FCSTD DOCUMENT  (FreeCAD 0.19R24366 (Git))
Label: master
License: All rights reserved
LicenseURL: http://en.wikipedia.org/wiki/All_rights_reserved
objects: Spreadsheet::Sheet×1

FEATURE [Spreadsheet::Sheet] Spreadsheet  label="inputs"
  cells = A1=Top Edge Padding; B1(top_edge_padding)==10.4775mm; A2=Left Edge Padding; B2(left_edge_padding)==top_edge_padding; A3=Right Edge Padding; B3(right_edge_padding)==top_edge_padding; A4=Bottom Edge Padding; B4(bottom_edge_padding)==top_edge_padding; A5=Edge Fillet Radius; B5(edge_fillet_radius)==2mm; A6=Key Width; B6(key_width)==14mm; A7=Key Height; B7(key_height)==key_width; A8=Horizontal Key Spacing; B8(horizontal_key_spacing)==5.05mm; A9=Vertical Key Spacing; B9(vertical_key_spacing)==horizontal_key_spacing; A10=Mounting Hole Diameter; B10(mounting_hole_diameter)==3.1mm; A11=Switch Layer Thickness; B11(switch_layer_thickness)==3mm; A12=PCB Fillet Radius; B12(pcb_fillet_radius)==2mm; A13=PCB Top Edge Padding; B13(pcb_top_edge_padding)==2.53mm; A14=PCB Left Edge Padding; B14(pcb_left_edge_padding)==pcb_top_edge_padding; A15=PCB Right Edge Padding; B15(pcb_right_edge_padding)==pcb_top_edge_padding; A16=PCB Bottom Edge Padding; B16(pcb_bottom_edge_padding)==pcb_top_edge_padding; A17=PCB Inner Bottom Edge Padding; B17(pcb_inner_bottom_edge_padding)==pcb_top_edge_padding; A18=PCB Inner Right Edge Padding; B18(pcb_inner_right_edge_padding)==pcb_top_edge_padding; A19=Hyperpixel Width; B19(hyperpixel_width)==98mm; A20=Hyperpixel Height	; B20(hyperpixel_height)==58.2mm; A21=Hyperpixel Depth; B21(hyperpixel_depth)==5.7mm; A22=Hyperpixel Screen Width; B22(hyperpixel_screen_width)==hyperpixel_width; A23=Hyperpixel Top Hole Padding; B23(hyperpixel_top_hole_padding)==4.5mm; A24=HyperPixel Bottom Hole Padding; B24(hyperpixel_bottom_hole_padding)==4.7mm; A25=Hyperpixel Left Hole Padding; B25(hyperpixel_left_hole_padding)==25mm; A26=Hyperpixel Right Hole Padding; B26(hyperpixel_right_hole_padding)==15mm; A27=Hyperpixel Standoff Height; B27(hyperpixel_standoff_height)==17mm; A28=Hyperpixel Standoff Diameter; B28(hyperpixel_standoff_diameter)==5mm; A29=Joystick Top Edge Padding; B29(joystick_top_edge_padding)==vertical_key_spacing; A30=Joystick Left Edge Padding; B30(joystick_left_edge_padding)==0mm; A31=Joystick Right Edge Padding; B31(joystick_right_edge_padding)==horizontal_key_spacing; A32=Joystick Bottom Edge Padding; B32(joystick_bottom_edge_padding)==0mm; A33=Encoder Spacing; B33(encoder_spacing)==7mm; A34=Wall Thickness; B34(wall_thickness)==7.144mm; A35=Lower Layer Thickness; B35(lower_layer_thickness)==3mm; A36=Raspberry Pi 4 Mounting Hole Diameter; B36(raspberry_pi_4_mounting_hole_diameter)==2.75mm; A37=Open Layer Thickness; B37(open_layer_thickness)==3mm; A38=Bottom Layer Thickness; B38(bottom_layer_thickness)==3mm; A39=Top Layer Thickness; B39(top_layer_thickness)==3mm; A40=Top Layer Thin Thickness; B40(top_layer_thin_thickness)==1.5mm; A41=Hyperpixel Screen Padding; B41(hyperpixel_screen_padding)==1mm; A42=3D Printed Switch Layer Thickness; B42(switch_layer_thickness_3D_print)==1.5mm; A43=Encoder Unthreaded Shaft Diameter; B43(encoder_unthreaded_shaft_diameter)==6mm; A44=Encoder Threaded Shaft Diameter; B44(encoder_threaded_shaft_diameter)==6.75mm; A45=Encoder Unthreaded Shaft Length; B45(encoder_unthreaded_shaft_length)==19.85mm; A46=Encoder Threaded Shaft Length; B46(encoder_threaded_shaft_length)==6.85mm; A47=Encoder Threaded Shaft Coverage; B47(encoder_threaded_shaft_coverage)=0.75; A48=Encoder Knob Diameter; B48(encoder_knob_diameter)==15mm; A49=Encoder Shaft Tolerance; B49(encoder_shaft_tolerance)==0.05mm; A50=Encoder Cap Length; B50(encoder_cap_length)==2mm; A51=Encoder Marker Width; B51(encoder_marker_width)==2mm; A52=Encoder Marker Depth; B52(encoder_marker_depth)==1mm; A53=Encoder Height; B53(encoder_height)==18mm; A54=Encoder Width; B54(encoder_width)==18mm; A55=Printer Tolerance; B55(printer_tolerance)==0.1mm
